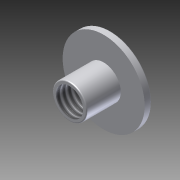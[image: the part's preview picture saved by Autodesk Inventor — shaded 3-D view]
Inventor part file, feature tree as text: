
AUTODESK INVENTOR PART (.ipt)
format: ipt  version: 2011 SP1 (Build 150282100, 282)  size: 118,272 bytes
history: native  units: in
note: dims shown in document units (in); Inventor stores cm internally (conversion verified against a paired STEP export)
features: extrude x2, fillet x2, sketch x2, hole x1, thread x1
ambient origin geometry x8: Origin, YZ Plane, XZ Plane, XY Plane, X Axis, Y Axis, Z Axis, Center Point
bodies: Solid1 (feature_tree)
feature tree (8):
  extrude  "Extrusion1"  Depth=0.0625in TaperAngle=0.0deg
  extrude  "Extrusion2"  Depth=0.3125in TaperAngle=0.0deg
  hole  "Hole1"  [1 undecoded]
  thread  "Thread1"  [1 undecoded]
  fillet  "Fillet1"  Radius=0.0625in
  fillet  "Fillet2"  Radius=0.01in
  sketch  "Sketch1"  dims[d0=0.75in d1=0.0625in d2=0.0in]
  sketch  "Sketch2"  dims[d3=0.3125in d4=0.3125in d5=0.0in d6=1.0in d7=1.0in d8=0.25in d9=0.75in d10=0.375in d11=0.25in d12=0.5635in d13=1.0in d14=0.8108in d15=1.0in d16=0.0in d17=0.0625in d18=0.01in]
note: 2 required parameter values undecoded (feature->parameter linkage not recoverable at this tier; creation-order binding heuristic only, values carry confidence <= 0.55)
